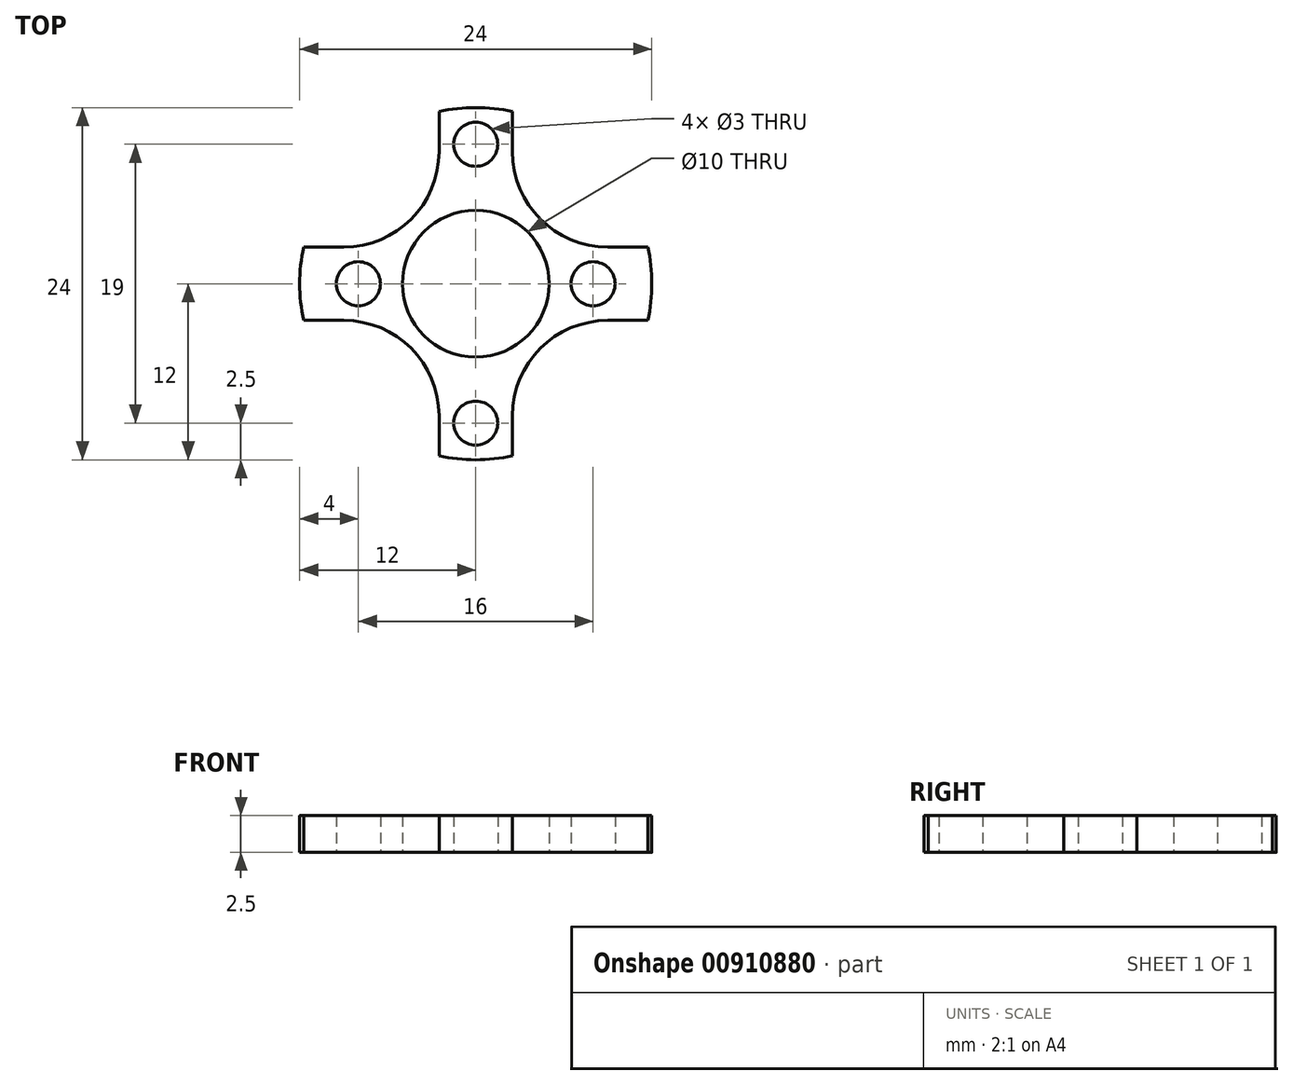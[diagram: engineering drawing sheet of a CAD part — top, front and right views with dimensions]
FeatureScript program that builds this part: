
annotation { "Feature Type Name" : "Feature", "Feature Type Description" : "" }
export const myFeature = defineFeature(function(context is Context, id is Id, definition is map)
    precondition{}
    {
        {
            var Q0;
            Q0=qCreatedBy(makeId("Top.planeOp"),FACE);
            var sketch = newSketch(context, id + "F0", { "sketchPlane" : qUnion([Q0])});
            skCircle(sketch, "E0", {"center": v(0, 0) * mm, "radius": 8 * mm, "construction": true});
            skCircle(sketch, "E1", {"center": v(0, 0) * mm, "radius": 9.5 * mm, "construction": true});
            skCircle(sketch, "E2", {"center": v(-8, 0) * mm, "radius": 1.5 * mm});
            skCircle(sketch, "E3", {"center": v(8, 0) * mm, "radius": 1.5 * mm});
            skCircle(sketch, "E4", {"center": v(0, 9.5) * mm, "radius": 1.5 * mm});
            skCircle(sketch, "E5", {"center": v(0, -9.5) * mm, "radius": 1.5 * mm});
            skLineSegment(sketch, "E6", {"start": v(0, 9.5) * mm, "end": v(-2.5, 9.5) * mm, "construction": true});
            skLineSegment(sketch, "E7", {"start": v(0, 9.5) * mm, "end": v(2.5, 9.5) * mm, "construction": true});
            skLineSegment(sketch, "E8", {"start": v(8, 0) * mm, "end": v(8, 2.5) * mm, "construction": true});
            skLineSegment(sketch, "E9", {"start": v(8, 0) * mm, "end": v(8, -2.5) * mm, "construction": true});
            skLineSegment(sketch, "E10", {"start": v(8, 0) * mm, "end": v(12, 0) * mm, "construction": true});
            skLineSegment(sketch, "E11", {"start": v(0, 9.5) * mm, "end": v(0, 12) * mm, "construction": true});
            skCircle(sketch, "E12", {"center": v(0, 0) * mm, "radius": 12 * mm, "construction": true});
            skLineSegment(sketch, "E13", {"start": v(-2.5, 9.5) * mm, "end": v(-2.5, 11.74) * mm});
            skLineSegment(sketch, "E14", {"start": v(2.5, 9.5) * mm, "end": v(2.5, 11.74) * mm});
            skLineSegment(sketch, "E15", {"start": v(9, 2.5) * mm, "end": v(11.74, 2.5) * mm});
            skLineSegment(sketch, "E16", {"start": v(9, -2.5) * mm, "end": v(11.74, -2.5) * mm});
            skArc(sketch, "E17", {"start": v(2.5, 11.74) * mm, "mid": v(0, 12) * mm, "end": v(-2.5, 11.74) * mm});
            skArc(sketch, "E18", {"start": v(11.74, -2.5) * mm, "mid": v(12, 0) * mm, "end": v(11.74, 2.5) * mm});
            skLineSegment(sketch, "E19", {"start": v(2.5, 9.5) * mm, "end": v(2.5, 0) * mm, "construction": true});
            skLineSegment(sketch, "E20", {"start": v(8, 2.5) * mm, "end": v(2.5, 2.5) * mm, "construction": true});
            skLineSegment(sketch, "E21", {"start": v(2.5, 9.5) * mm, "end": v(2.5, 9) * mm});
            skPoint(sketch, "E22.visualSharp", {"position": v(2.5, 2.5) * mm});
            skArc(sketch, "E22.filletArc", {"start": v(2.5, 9) * mm, "mid": v(4.4, 4.4) * mm, "end": v(9, 2.5) * mm});
            skLineSegment(sketch, "E23", {"start": v(0, 0) * mm, "end": v(4.42, 4.42) * mm, "construction": true});
            skLineSegment(sketch, "E24.MirrorCS", {"start": v(-9, -2.5) * mm, "end": v(-11.74, -2.5) * mm});
            skArc(sketch, "E25.MirrorCS", {"start": v(-11.74, -2.5) * mm, "mid": v(-12, 0) * mm, "end": v(-11.74, 2.5) * mm});
            skLineSegment(sketch, "E26.MirrorCS", {"start": v(-2.5, 9.5) * mm, "end": v(-2.5, 9) * mm});
            skLineSegment(sketch, "E27.MirrorCS", {"start": v(-9, 2.5) * mm, "end": v(-11.74, 2.5) * mm});
            skArc(sketch, "E28.MirrorCS", {"start": v(-2.5, 9) * mm, "mid": v(-4.4, 4.4) * mm, "end": v(-9, 2.5) * mm});
            skPoint(sketch, "E29.orphan", {"position": v(-8, 2.5) * mm});
            skLineSegment(sketch, "E30.MirrorCS", {"start": v(-2.5, -9.5) * mm, "end": v(-2.5, -11.74) * mm});
            skArc(sketch, "E31.MirrorCS", {"start": v(2.5, -11.74) * mm, "mid": v(0, -12) * mm, "end": v(-2.5, -11.74) * mm});
            skLineSegment(sketch, "E32.MirrorCS", {"start": v(2.5, -9.5) * mm, "end": v(2.5, -11.74) * mm});
            skArc(sketch, "E33.MirrorCS", {"start": v(2.5, -9) * mm, "mid": v(4.4, -4.4) * mm, "end": v(9, -2.5) * mm});
            skLineSegment(sketch, "E34.MirrorCS", {"start": v(-2.5, -9.5) * mm, "end": v(-2.5, -9) * mm});
            skLineSegment(sketch, "E35.MirrorCS", {"start": v(2.5, -9.5) * mm, "end": v(2.5, -9) * mm});
            skArc(sketch, "E36.MirrorCS", {"start": v(-2.5, -9) * mm, "mid": v(-4.4, -4.4) * mm, "end": v(-9, -2.5) * mm});
            skPoint(sketch, "E37.orphan", {"position": v(-8, -2.5) * mm});
            skCircle(sketch, "E38", {"center": v(0, 0) * mm, "radius": 5 * mm});
            skSolve(sketch);
        }
        {
            var Q0;
            Q0 = qSketchRegion(id + "F0", true);
            extrude(context, id + "F1", {"entities" : qUnion([Q0]), "depth" : 2.5 * mm, "offsetDistance" : 25 * mm});
        }
    });
